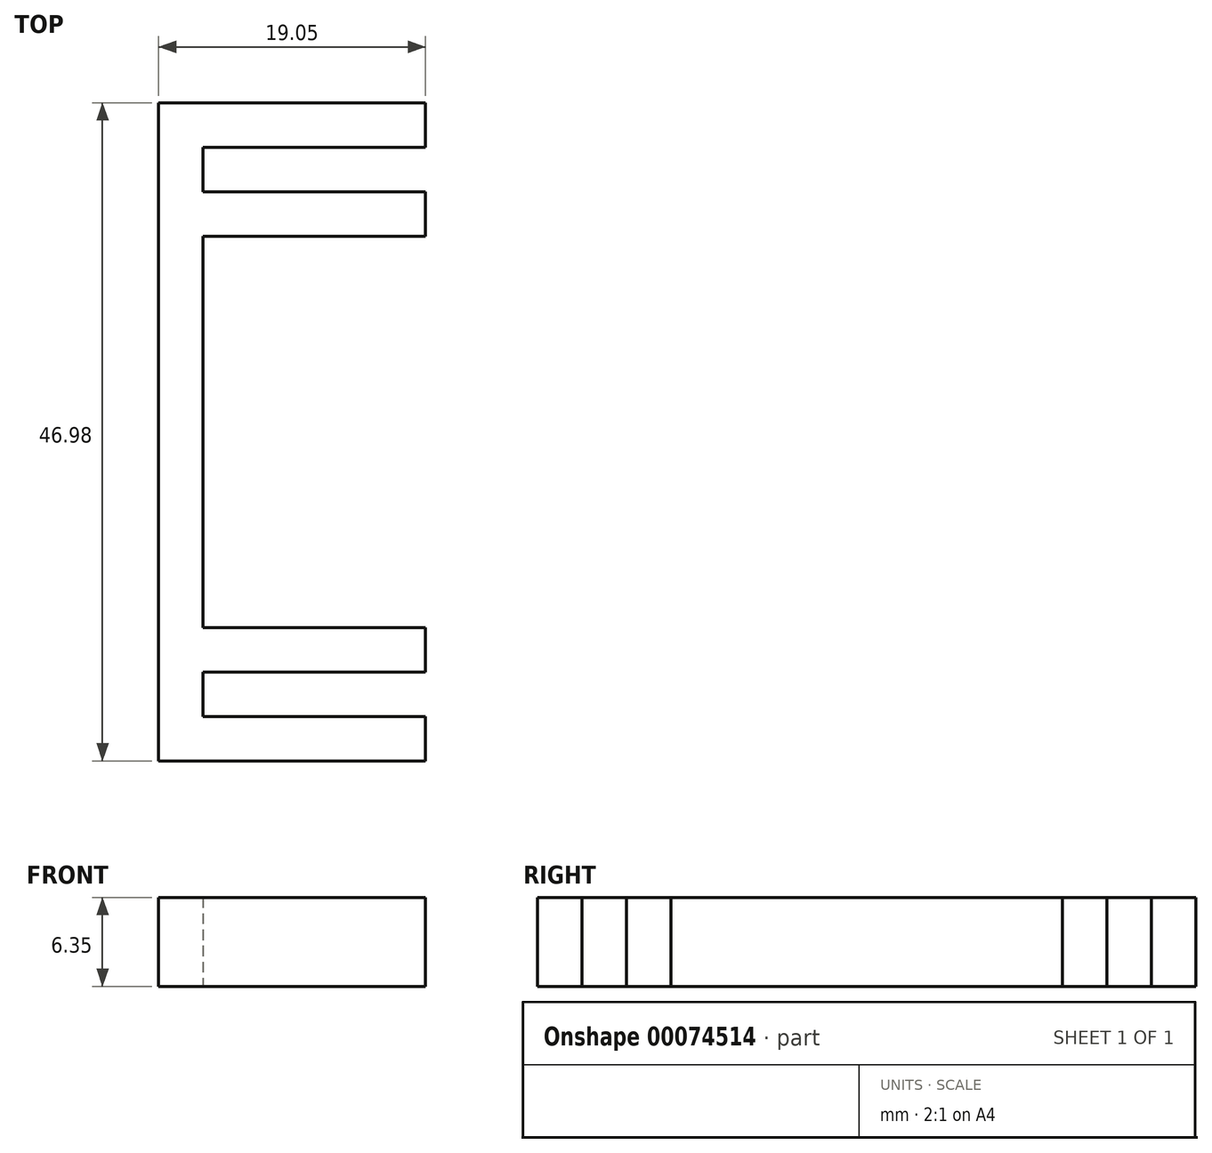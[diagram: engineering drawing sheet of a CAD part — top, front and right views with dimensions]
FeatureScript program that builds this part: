
annotation { "Feature Type Name" : "Feature", "Feature Type Description" : "" }
export const myFeature = defineFeature(function(context is Context, id is Id, definition is map)
    precondition{}
    {
        {
            var Q0;
            Q0=qCreatedBy(makeId("Top.planeOp"),FACE);
            var sketch = newSketch(context, id + "F0", { "sketchPlane" : qUnion([Q0])});
            skLineSegment(sketch, "E0.bottom", {"start": v(0, 0) * mm, "end": v(3.17, 0) * mm});
            skLineSegment(sketch, "E0.top", {"start": v(0, 40.64) * mm, "end": v(3.17, 40.64) * mm});
            skLineSegment(sketch, "E0.left", {"start": v(0, 0) * mm, "end": v(0, 40.64) * mm});
            skLineSegment(sketch, "E0.right", {"start": v(3.17, 0) * mm, "end": v(3.17, 40.64) * mm});
            skLineSegment(sketch, "E1.bottom", {"start": v(0, 40.64) * mm, "end": v(19.05, 40.64) * mm});
            skLineSegment(sketch, "E1.top", {"start": v(0, 43.82) * mm, "end": v(19.05, 43.82) * mm});
            skLineSegment(sketch, "E1.left", {"start": v(0, 40.64) * mm, "end": v(0, 43.82) * mm});
            skLineSegment(sketch, "E1.right", {"start": v(19.05, 40.64) * mm, "end": v(19.05, 43.82) * mm});
            skLineSegment(sketch, "E2.bottom", {"start": v(0, 0) * mm, "end": v(19.05, 0) * mm});
            skLineSegment(sketch, "E2.top", {"start": v(0, -3.18) * mm, "end": v(19.05, -3.18) * mm});
            skLineSegment(sketch, "E2.left", {"start": v(0, 0) * mm, "end": v(0, -3.18) * mm});
            skLineSegment(sketch, "E2.right", {"start": v(19.05, 0) * mm, "end": v(19.05, -3.18) * mm});
            skLineSegment(sketch, "E3.bottom", {"start": v(3.18, 3.18) * mm, "end": v(19.05, 3.18) * mm});
            skLineSegment(sketch, "E3.top", {"start": v(3.18, 6.35) * mm, "end": v(19.05, 6.35) * mm});
            skLineSegment(sketch, "E3.left", {"start": v(3.17, 3.18) * mm, "end": v(3.17, 6.35) * mm});
            skLineSegment(sketch, "E3.right", {"start": v(19.05, 3.17) * mm, "end": v(19.05, 6.35) * mm});
            skLineSegment(sketch, "E4.bottom", {"start": v(3.17, 34.3) * mm, "end": v(19.05, 34.3) * mm});
            skLineSegment(sketch, "E4.top", {"start": v(3.17, 37.47) * mm, "end": v(19.05, 37.47) * mm});
            skLineSegment(sketch, "E4.left", {"start": v(3.17, 34.3) * mm, "end": v(3.17, 37.47) * mm});
            skLineSegment(sketch, "E4.right", {"start": v(19.05, 34.3) * mm, "end": v(19.05, 37.47) * mm});
            skSolve(sketch);
        }
        {
            var Q0;
            Q0=makeQuery(id+"F0.imprint","IMPRINT",FACE,{"disambiguationData":[TD([[makeQuery(id+"F0.imprint","IMPRINT",EDGE,{"derivedFrom":sQuery(id+"F0.wireOp",EDGE,"E1.top")}),-1.0]])]});
            var Q1;
            {var subQ6=sQuery(id+"F0.wireOp",EDGE,"E0.left");Q1=makeQuery(id+"F0.imprint","IMPRINT",FACE,{"disambiguationData":[TD([[makeQuery(id+"F0.imprint","IMPRINT",EDGE,{"derivedFrom":subQ6}),-1.0]])]});}
            var Q2;
            Q2=makeQuery(id+"F0.imprint","IMPRINT",FACE,{"disambiguationData":[TD([[makeQuery(id+"F0.imprint","IMPRINT",EDGE,{"derivedFrom":sQuery(id+"F0.wireOp",EDGE,"E4.bottom")}),1.0]])]});
            var Q3;
            Q3=makeQuery(id+"F0.imprint","IMPRINT",FACE,{"disambiguationData":[TD([[makeQuery(id+"F0.imprint","IMPRINT",EDGE,{"derivedFrom":sQuery(id+"F0.wireOp",EDGE,"E3.bottom")}),1.0]])]});
            var Q4;
            Q4=makeQuery(id+"F0.imprint","IMPRINT",FACE,{"disambiguationData":[TD([[makeQuery(id+"F0.imprint","IMPRINT",EDGE,{"derivedFrom":sQuery(id+"F0.wireOp",EDGE,"E2.top")}),1.0]])]});
            extrude(context, id + "F1", {"entities" : qUnion([Q0, Q1, Q2, Q3, Q4]), "depth" : 6.35 * mm});
        }
    });
